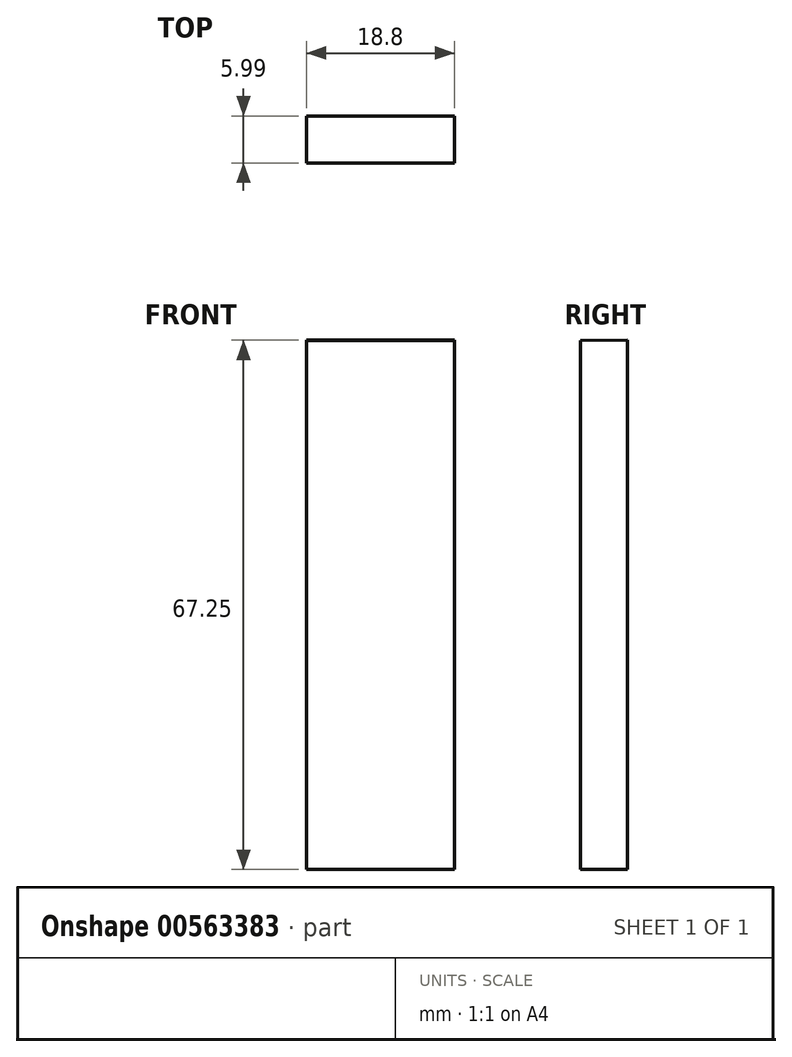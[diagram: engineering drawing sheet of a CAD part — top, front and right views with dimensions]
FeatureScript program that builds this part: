
annotation { "Feature Type Name" : "Feature", "Feature Type Description" : "" }
export const myFeature = defineFeature(function(context is Context, id is Id, definition is map)
    precondition{}
    {
        {
            var Q0;
            Q0=qCreatedBy(makeId("Right.planeOp"),FACE);
            var sketch = newSketch(context, id + "F0", { "sketchPlane" : qUnion([Q0])});
            skLineSegment(sketch, "E0", {"start": v(-36.65, 75.1) * mm, "end": v(-36.65, 7.92) * mm});
            skLineSegment(sketch, "E1", {"start": v(-36.65, 7.92) * mm, "end": v(-30.66, 7.92) * mm});
            skLineSegment(sketch, "E2", {"start": v(-30.66, 7.92) * mm, "end": v(-30.66, 75.17) * mm});
            skLineSegment(sketch, "E3", {"start": v(-30.66, 75.17) * mm, "end": v(-36.65, 75.1) * mm});
            skSolve(sketch);
        }
        {
            var Q0;
            Q0=qSketchRegion(id+"F0",true);
            extrude(context, id + "F1", {"entities" : qUnion([Q0]), "depth" : 18.8 * mm});
        }
    });
